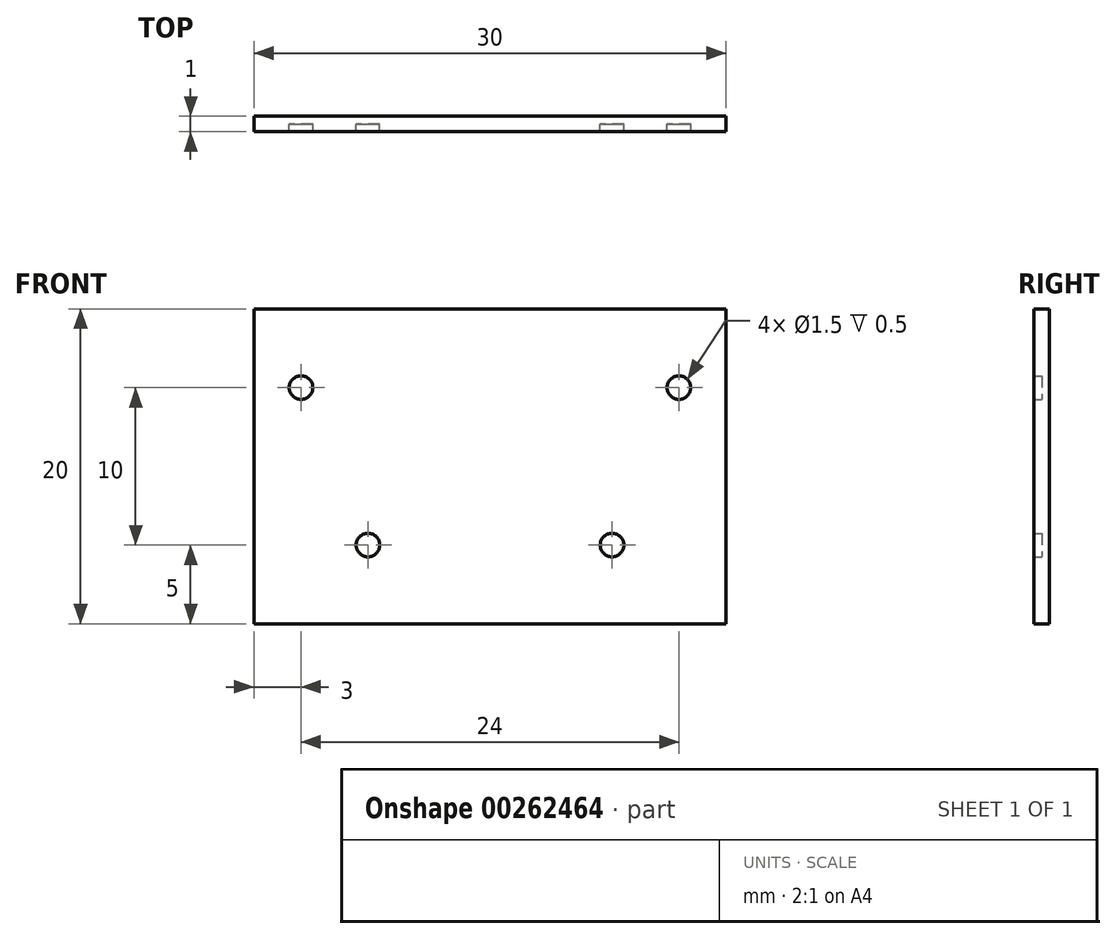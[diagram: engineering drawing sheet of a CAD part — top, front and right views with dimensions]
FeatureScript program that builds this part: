
annotation { "Feature Type Name" : "Feature", "Feature Type Description" : "" }
export const myFeature = defineFeature(function(context is Context, id is Id, definition is map)
    precondition{}
    {
        {
            var Q0;
            Q0=qCreatedBy(makeId("Front.planeOp"),FACE);
            var sketch = newSketch(context, id + "F0", { "sketchPlane" : qUnion([Q0])});
            skLineSegment(sketch, "E0.bottom", {"start": v(15, 10) * mm, "end": v(-15, 10) * mm});
            skLineSegment(sketch, "E0.top", {"start": v(15, -10) * mm, "end": v(-15, -10) * mm});
            skLineSegment(sketch, "E0.left", {"start": v(15, 10) * mm, "end": v(15, -10) * mm});
            skLineSegment(sketch, "E0.right", {"start": v(-15, 10) * mm, "end": v(-15, -10) * mm});
            skPoint(sketch, "E0.middle", {"position": v(0, 0) * mm});
            skPoint(sketch, "E1", {"position": v(-7.75, -5) * mm});
            skPoint(sketch, "E2", {"position": v(7.75, -5) * mm});
            skPoint(sketch, "E3", {"position": v(12, 5) * mm});
            skPoint(sketch, "E4", {"position": v(-12, 5) * mm});
            skLineSegment(sketch, "E5", {"start": v(-12, 5) * mm, "end": v(12, 5) * mm, "construction": true});
            skPoint(sketch, "E6", {"position": v(0, 5) * mm});
            skLineSegment(sketch, "E7", {"start": v(-7.75, -5) * mm, "end": v(7.75, -5) * mm, "construction": true});
            skLineSegment(sketch, "E8", {"start": v(0, 5) * mm, "end": v(0, -5) * mm, "construction": true});
            skSolve(sketch);
        }
        {
            var Q0;
            Q0 = qSketchRegion(id + "F0", true);
            extrude(context, id + "F1", {"entities" : qUnion([Q0]), "endBound" : BoundingType.SYMMETRIC, "depth" : 1 * mm});
        }
        {
            var Q0;
            Q0=sQuery(id+"F0.wireOp",VERTEX,"E4");
            var Q1;
            Q1=sQuery(id+"F0.wireOp",VERTEX,"E3");
            var Q2;
            Q2=sQuery(id+"F0.wireOp",VERTEX,"E2");
            var Q3;
            Q3=sQuery(id+"F0.wireOp",VERTEX,"E1");
            var Q4;
            Q4=makeQuery(id+"F1.opExtrude","SWEPT_BODY",BODY,{"disambiguationData":[OSD([sQuery(id+"F0.wireOp",EDGE,"E0.bottom"),sQuery(id+"F0.wireOp",EDGE,"E0.top"),sQuery(id+"F0.wireOp",EDGE,"E0.left"),sQuery(id+"F0.wireOp",EDGE,"E0.right")])]});
            hole(context, id + "F2", {"style" : HoleStyle.SIMPLE, "endStyle" : HoleEndStyle.THROUGH, "oppositeDirection" : true, "holeDiameter" : 1.5 * mm, "tappedDepth" : 12 * mm, "tapClearance" : 3, "locations" : qUnion([Q0, Q1, Q2, Q3]), "scope" : qUnion([Q4])});
        }
    });
